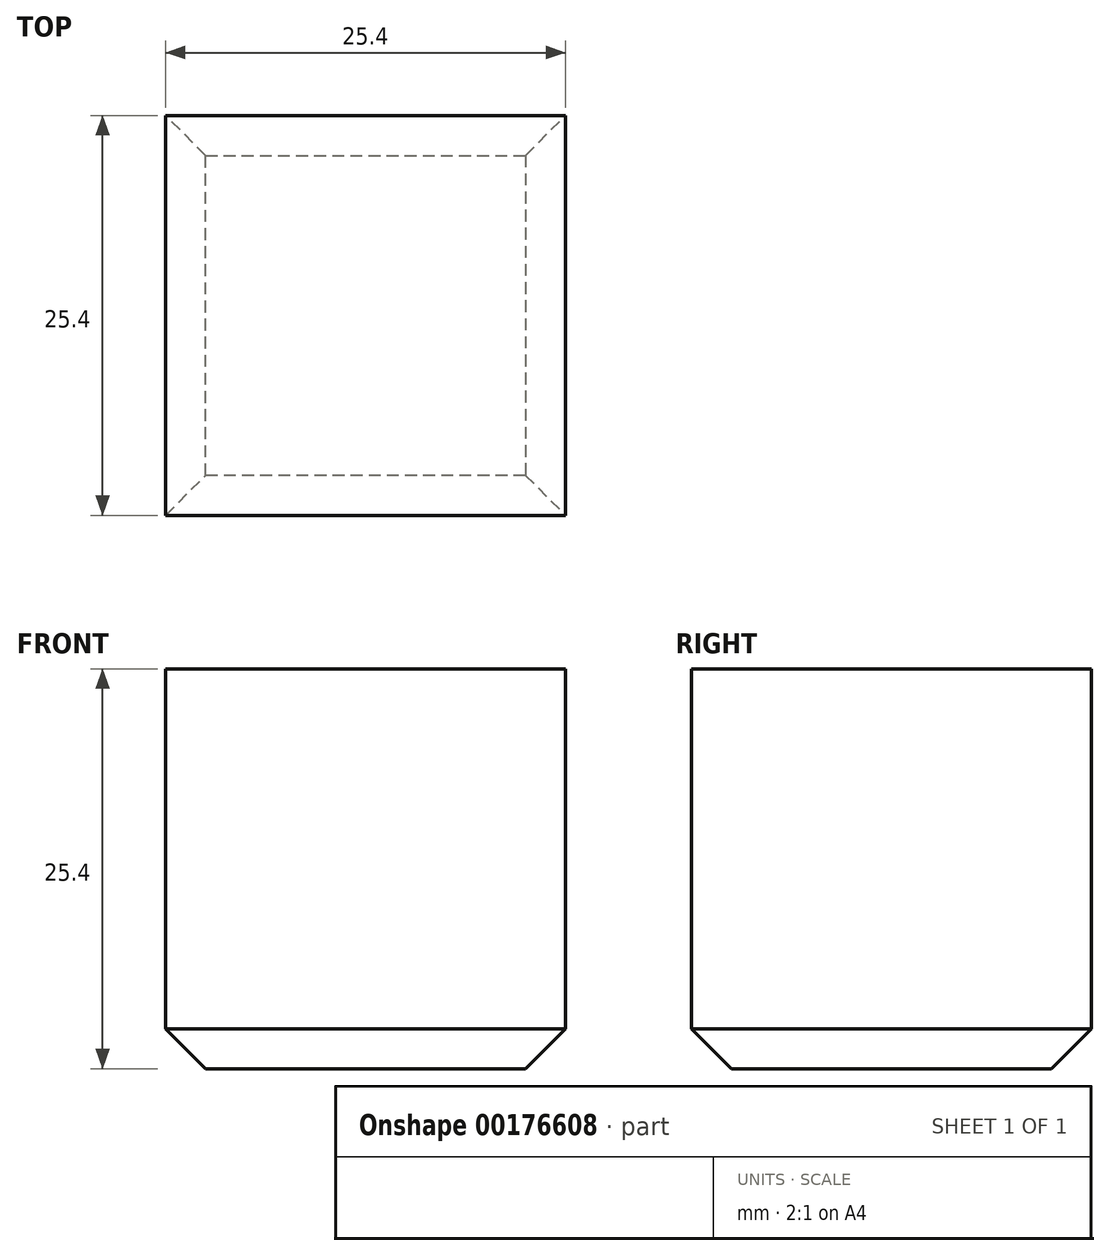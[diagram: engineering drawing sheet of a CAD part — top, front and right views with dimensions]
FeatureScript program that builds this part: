
annotation { "Feature Type Name" : "Feature", "Feature Type Description" : "" }
export const myFeature = defineFeature(function(context is Context, id is Id, definition is map)
    precondition{}
    {
        {
            var Q0;
            Q0=qCreatedBy(makeId("Top.planeOp"),FACE);
            var sketch = newSketch(context, id + "F0", { "sketchPlane" : qUnion([Q0])});
            skLineSegment(sketch, "E0.bottom", {"start": v(0, 0) * mm, "end": v(25.4, 0) * mm});
            skLineSegment(sketch, "E0.top", {"start": v(0, 25.4) * mm, "end": v(25.4, 25.4) * mm});
            skLineSegment(sketch, "E0.left", {"start": v(0, 0) * mm, "end": v(0, 25.4) * mm});
            skLineSegment(sketch, "E0.right", {"start": v(25.4, 0) * mm, "end": v(25.4, 25.4) * mm});
            skSolve(sketch);
        }
        {
            var Q0;
            Q0=makeQuery(id+"F0.imprint","IMPRINT",FACE,{"disambiguationData":[TD([[makeQuery(id+"F0.imprint","IMPRINT",EDGE,{"derivedFrom":sQuery(id+"F0.wireOp",EDGE,"E0.bottom")}),1.0]])]});
            extrude(context, id + "F1", {"entities" : qUnion([Q0]), "depth" : 25.4 * mm});
        }
        {
            var Q0;
            Q0=makeQuery(id+"F1.opExtrude","CAP_EDGE",EDGE,{"disambiguationData":[OSD([sQuery(id+"F0.wireOp",EDGE,"E0.bottom")])],"isStart":true});
            var Q1;
            Q1=makeQuery(id+"F1.opExtrude","CAP_EDGE",EDGE,{"disambiguationData":[OSD([sQuery(id+"F0.wireOp",EDGE,"E0.right")])],"isStart":true});
            var Q2;
            Q2=makeQuery(id+"F1.opExtrude","CAP_EDGE",EDGE,{"disambiguationData":[OSD([sQuery(id+"F0.wireOp",EDGE,"E0.left")])],"isStart":true});
            var Q3;
            Q3=makeQuery(id+"F1.opExtrude","CAP_EDGE",EDGE,{"disambiguationData":[OSD([sQuery(id+"F0.wireOp",EDGE,"E0.top")])],"isStart":true});
            chamfer(context, id + "F2", {"entities" : qUnion([Q0, Q1, Q2, Q3]), "width" : 2.54 * mm, "tangentPropagation" : true});
        }
    });
